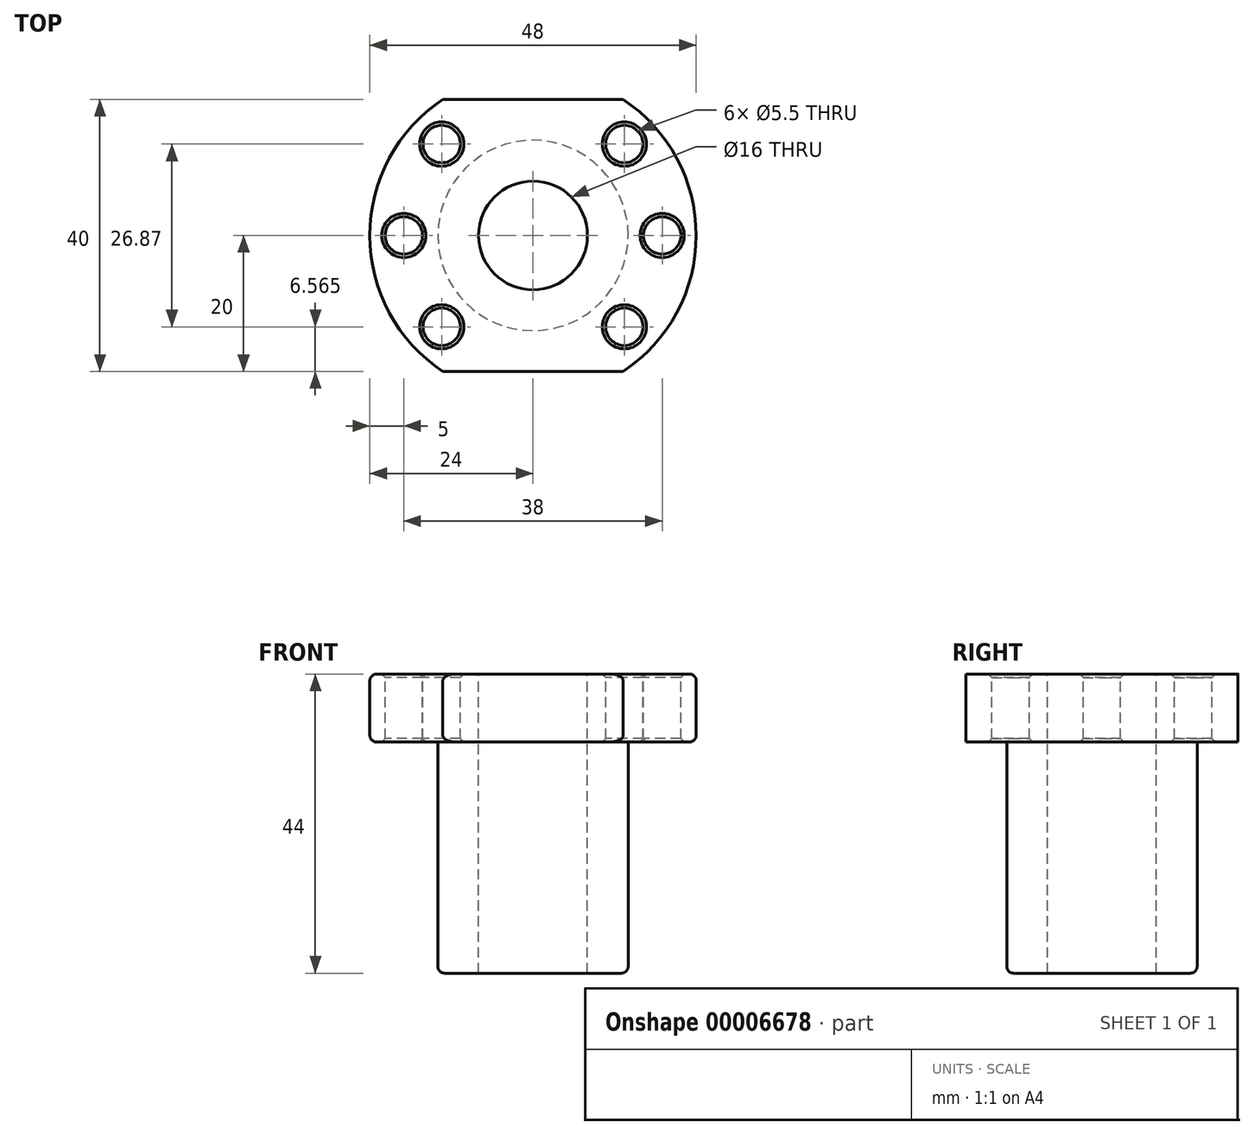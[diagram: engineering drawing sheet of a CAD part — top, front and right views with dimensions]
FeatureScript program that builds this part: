
annotation { "Feature Type Name" : "Feature", "Feature Type Description" : "" }
export const myFeature = defineFeature(function(context is Context, id is Id, definition is map)
    precondition{}
    {
        {
            var Q0;
            Q0=qCreatedBy(makeId("Top.planeOp"),FACE);
            var sketch = newSketch(context, id + "F0", { "sketchPlane" : qUnion([Q0])});
            skCircle(sketch, "E0", {"center": v(0, 0) * mm, "radius": 14 * mm});
            skSolve(sketch);
        }
        {
            var Q0;
            Q0 = qSketchRegion(id + "F0", true);
            extrude(context, id + "F1", {"entities" : qUnion([Q0]), "depth" : 34 * mm});
        }
        {
            var Q0;
            Q0=makeQuery(id+"F1.opExtrude","CAP_FACE",FACE,{"disambiguationData":[OSD([sQuery(id+"F0.wireOp",EDGE,"E0")])],"isStart":false});
            var sketch = newSketch(context, id + "F2", { "sketchPlane" : qUnion([Q0])});
            skCircle(sketch, "E1", {"center": v(0, 0) * mm, "radius": 24 * mm});
            skSolve(sketch);
        }
        {
            var Q0;
            Q0 = qSketchRegion(id + "F2", true);
            extrude(context, id + "F3", {"entities" : qUnion([Q0]), "operationType" : NewBodyOperationType.ADD, "depth" : 10 * mm});
        }
        {
            var Q0;
            Q0=makeQuery(id+"F3.opExtrude","CAP_FACE",FACE,{"disambiguationData":[OSD([sQuery(id+"F2.wireOp",EDGE,"E1")])],"isStart":false});
            var sketch = newSketch(context, id + "F4", { "sketchPlane" : qUnion([Q0])});
            skLineSegment(sketch, "E2.0", {"start": v(-13.27, -20) * mm, "end": v(13.27, -20) * mm});
            skLineSegment(sketch, "E3.0", {"start": v(-13.27, 20) * mm, "end": v(13.27, 20) * mm});
            skArc(sketch, "E4", {"start": v(13.27, 20) * mm, "mid": v(0, 24) * mm, "end": v(-13.27, 20) * mm});
            skArc(sketch, "E5.trimOffspring", {"start": v(-13.27, -20) * mm, "mid": v(0, -24) * mm, "end": v(13.27, -20) * mm});
            skSolve(sketch);
        }
        {
            var Q0;
            Q0 = qSketchRegion(id + "F4", true);
            extrude(context, id + "F5", {"entities" : qUnion([Q0]), "operationType" : NewBodyOperationType.REMOVE, "oppositeDirection" : true, "depth" : 10 * mm});
        }
        {
            var Q0;
            Q0=makeQuery(id+"F3.opExtrude","CAP_FACE",FACE,{"disambiguationData":[OSD([sQuery(id+"F2.wireOp",EDGE,"E1")])],"isStart":false});
            var sketch = newSketch(context, id + "F6", { "sketchPlane" : qUnion([Q0])});
            skCircle(sketch, "E6", {"center": v(-19, 0) * mm, "radius": 2.75 * mm});
            skLineSegment(sketch, "E7", {"start": v(-19, 0) * mm, "end": v(24, 0) * mm, "construction": true});
            skLineSegment(sketch, "E8", {"start": v(13.44, -13.44) * mm, "end": v(-13.44, 13.44) * mm, "construction": true});
            skLineSegment(sketch, "E9", {"start": v(0, 20) * mm, "end": v(0, -20) * mm, "construction": true});
            skLineSegment(sketch, "E10", {"start": v(-13.44, -13.44) * mm, "end": v(13.44, 13.44) * mm, "construction": true});
            skCircle(sketch, "E11", {"center": v(-13.44, 13.44) * mm, "radius": 2.75 * mm});
            skCircle(sketch, "E12", {"center": v(13.44, 13.44) * mm, "radius": 2.75 * mm});
            skCircle(sketch, "E13", {"center": v(19, 0) * mm, "radius": 2.75 * mm});
            skCircle(sketch, "E14", {"center": v(13.44, -13.44) * mm, "radius": 2.75 * mm});
            skCircle(sketch, "E15", {"center": v(-13.44, -13.44) * mm, "radius": 2.75 * mm});
            skSolve(sketch);
        }
        {
            var Q0;
            Q0 = qSketchRegion(id + "F6", true);
            extrude(context, id + "F7", {"entities" : qUnion([Q0]), "operationType" : NewBodyOperationType.REMOVE, "oppositeDirection" : true, "depth" : 10 * mm});
        }
        {
            var Q0;
            Q0=makeQuery(id+"F5.boolean.opBoolean","SPLIT",EDGE,{"disambiguationData":[OD(0.0)],"derivedFrom":makeQuery(id+"F3.opExtrude","CAP_EDGE",EDGE,{"disambiguationData":[OSD([sQuery(id+"F2.wireOp",EDGE,"E1")])],"isStart":false})});
            var Q1;
            Q1=makeQuery(id+"F5.boolean.opBoolean","SPLIT",EDGE,{"disambiguationData":[OD(0.0)],"derivedFrom":makeQuery(id+"F3.opExtrude","CAP_EDGE",EDGE,{"disambiguationData":[OSD([sQuery(id+"F2.wireOp",EDGE,"E1")])],"isStart":true})});
            var Q2;
            Q2=makeQuery(id+"F5.boolean.opBoolean","SPLIT",EDGE,{"disambiguationData":[OD(1.0)],"derivedFrom":makeQuery(id+"F3.opExtrude","CAP_EDGE",EDGE,{"disambiguationData":[OSD([sQuery(id+"F2.wireOp",EDGE,"E1")])],"isStart":false})});
            var Q3;
            Q3=makeQuery(id+"F5.boolean.opBoolean","SPLIT",EDGE,{"disambiguationData":[OD(1.0)],"derivedFrom":makeQuery(id+"F3.opExtrude","CAP_EDGE",EDGE,{"disambiguationData":[OSD([sQuery(id+"F2.wireOp",EDGE,"E1")])],"isStart":true})});
            var Q4;
            Q4=makeQuery(id+"F1.opExtrude","CAP_EDGE",EDGE,{"disambiguationData":[OSD([sQuery(id+"F0.wireOp",EDGE,"E0")])],"isStart":true});
            fillet(context, id + "F8", {"entities" : qUnion([Q0, Q1, Q2, Q3, Q4]), "radius" : 1 * mm, "allowEdgeOverflow" : false});
        }
        {
            var Q0;
            Q0=makeQuery(id+"F7.boolean.opBoolean","COPY",FACE,{"derivedFrom":makeQuery(id+"F7.opExtrude","SWEPT_FACE",FACE,{"disambiguationData":[OSD([sQuery(id+"F6.wireOp",EDGE,"E6")])]})});
            var Q1;
            Q1=makeQuery(id+"F7.boolean.opBoolean","COPY",FACE,{"derivedFrom":makeQuery(id+"F7.opExtrude","SWEPT_FACE",FACE,{"disambiguationData":[OSD([sQuery(id+"F6.wireOp",EDGE,"E11")])]})});
            var Q2;
            Q2=makeQuery(id+"F7.boolean.opBoolean","COPY",FACE,{"derivedFrom":makeQuery(id+"F7.opExtrude","SWEPT_FACE",FACE,{"disambiguationData":[OSD([sQuery(id+"F6.wireOp",EDGE,"E15")])]})});
            var Q3;
            Q3=makeQuery(id+"F7.boolean.opBoolean","COPY",FACE,{"derivedFrom":makeQuery(id+"F7.opExtrude","SWEPT_FACE",FACE,{"disambiguationData":[OSD([sQuery(id+"F6.wireOp",EDGE,"E14")])]})});
            var Q4;
            Q4=makeQuery(id+"F7.boolean.opBoolean","COPY",FACE,{"derivedFrom":makeQuery(id+"F7.opExtrude","SWEPT_FACE",FACE,{"disambiguationData":[OSD([sQuery(id+"F6.wireOp",EDGE,"E13")])]})});
            var Q5;
            Q5=makeQuery(id+"F7.boolean.opBoolean","COPY",FACE,{"derivedFrom":makeQuery(id+"F7.opExtrude","SWEPT_FACE",FACE,{"disambiguationData":[OSD([sQuery(id+"F6.wireOp",EDGE,"E12")])]})});
            chamfer(context, id + "F9", {"entities" : qUnion([Q0, Q1, Q2, Q3, Q4, Q5]), "width" : 0.5 * mm, "tangentPropagation" : true});
        }
        {
            var Q0;
            Q0=makeQuery(id+"F3.opExtrude","CAP_FACE",FACE,{"disambiguationData":[OSD([sQuery(id+"F2.wireOp",EDGE,"E1")])],"isStart":false});
            var sketch = newSketch(context, id + "F10", { "sketchPlane" : qUnion([Q0])});
            skCircle(sketch, "E16", {"center": v(0, 0) * mm, "radius": 8 * mm});
            skSolve(sketch);
        }
        {
            var Q0;
            Q0 = qSketchRegion(id + "F10", true);
            extrude(context, id + "F11", {"entities" : qUnion([Q0]), "operationType" : NewBodyOperationType.REMOVE, "endBound" : BoundingType.THROUGH_ALL, "oppositeDirection" : true, "depth" : 25 * mm});
        }
    });
